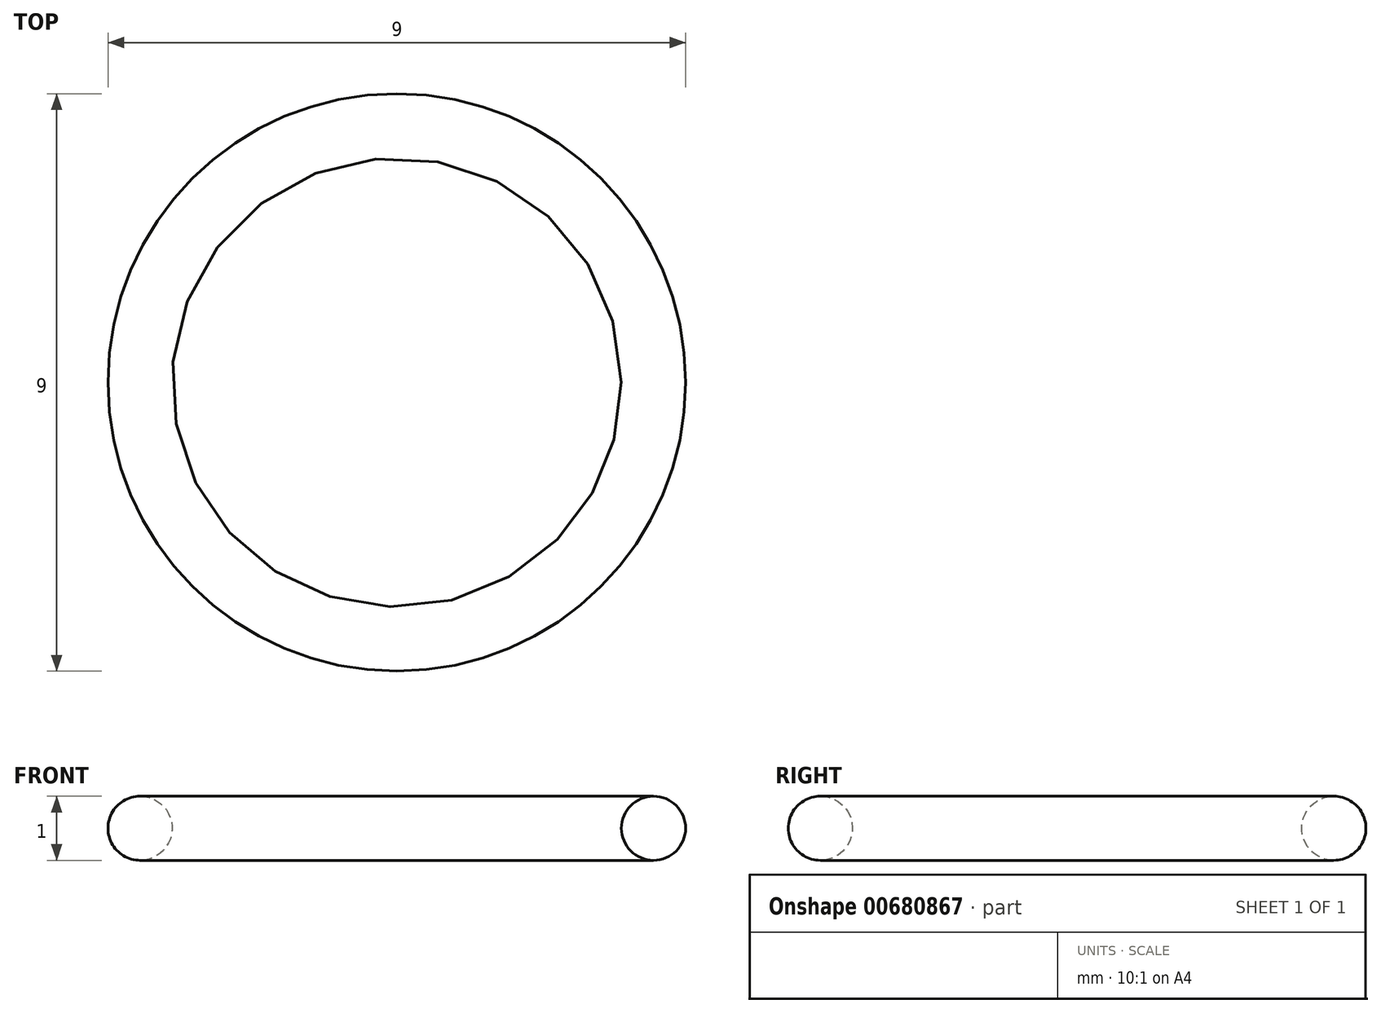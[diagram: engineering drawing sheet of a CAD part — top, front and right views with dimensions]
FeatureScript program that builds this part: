
annotation { "Feature Type Name" : "Feature", "Feature Type Description" : "" }
export const myFeature = defineFeature(function(context is Context, id is Id, definition is map)
    precondition{}
    {
        {
            var Q0;
            Q0=qCreatedBy(makeId("Front.planeOp"),FACE);
            var sketch = newSketch(context, id + "F0", { "sketchPlane" : qUnion([Q0])});
            skCircle(sketch, "E0", {"center": v(-4, 0) * mm, "radius": 0.5 * mm});
            skLineSegment(sketch, "E1", {"start": v(0, 5.5) * mm, "end": v(0, -4.96) * mm});
            skSolve(sketch);
        }
        {
            var Q0;
            Q0=makeQuery(id+"F0.imprint","IMPRINT",FACE,{"disambiguationData":[TD([[makeQuery(id+"F0.imprint","IMPRINT",EDGE,{"derivedFrom":sQuery(id+"F0.wireOp",EDGE,"E0")}),1.0]])]});
            var Q1;
            Q1=sQuery(id+"F0.wireOp",EDGE,"E1");
            revolve(context, id + "F1", {"entities" : qUnion([Q0]), "axis" : qUnion([Q1]), "revolveType" : RevolveType.FULL});
        }
    });
